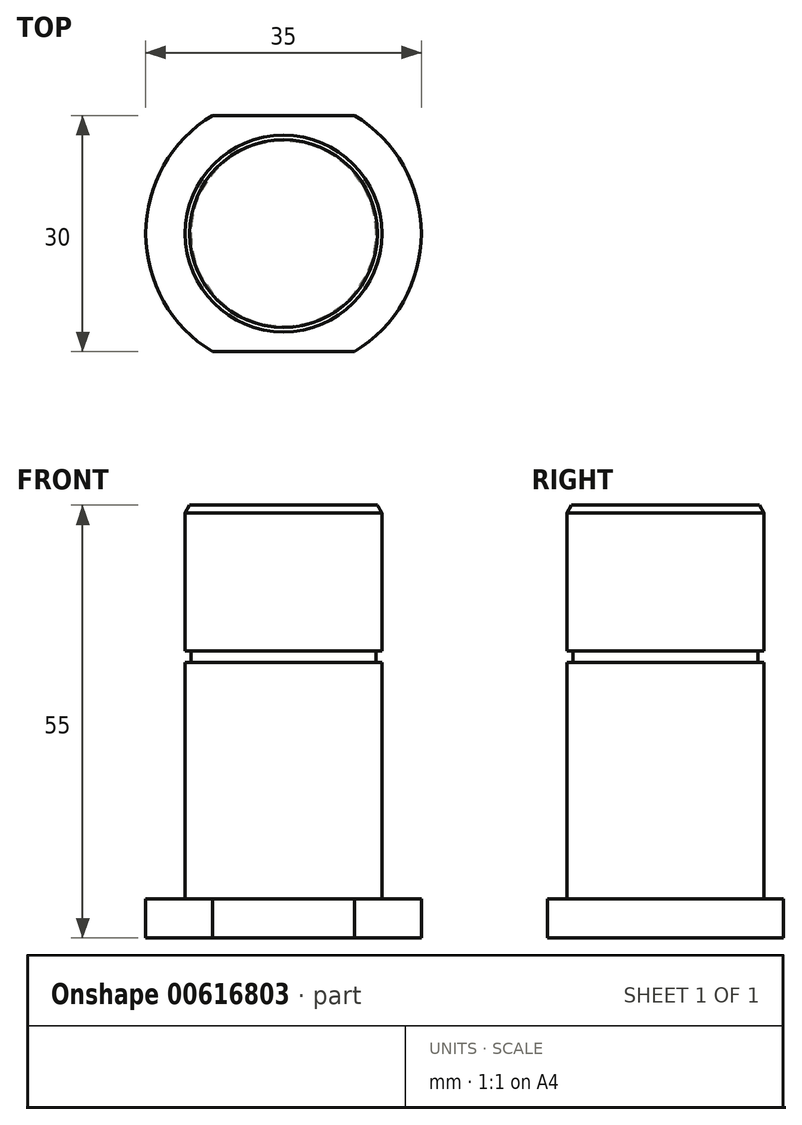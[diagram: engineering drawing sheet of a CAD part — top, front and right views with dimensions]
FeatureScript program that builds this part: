
annotation { "Feature Type Name" : "Feature", "Feature Type Description" : "" }
export const myFeature = defineFeature(function(context is Context, id is Id, definition is map)
    precondition{}
    {
        {
            var Q0;
            Q0=qCreatedBy(makeId("Top.planeOp"),FACE);
            var sketch = newSketch(context, id + "F0", { "sketchPlane" : qUnion([Q0])});
            skCircle(sketch, "E0", {"center": v(0, 0) * mm, "radius": 17.5 * mm});
            skSolve(sketch);
        }
        {
            var Q0;
            Q0 = qSketchRegion(id + "F0", true);
            extrude(context, id + "F1", {"entities" : qUnion([Q0]), "depth" : 5 * mm, "offsetDistance" : 25 * mm});
        }
        {
            var Q0;
            Q0=makeQuery(id+"F1.opExtrude","CAP_FACE",FACE,{"disambiguationData":[OSD([sQuery(id+"F0.wireOp",EDGE,"E0")])],"isStart":false});
            var sketch = newSketch(context, id + "F2", { "sketchPlane" : qUnion([Q0])});
            skCircle(sketch, "E1", {"center": v(0, 0) * mm, "radius": 12.5 * mm});
            skSolve(sketch);
        }
        {
            var Q0;
            Q0 = qSketchRegion(id + "F2", true);
            extrude(context, id + "F3", {"entities" : qUnion([Q0]), "operationType" : NewBodyOperationType.ADD, "depth" : 50 * mm, "offsetDistance" : 25 * mm});
        }
        {
            var Q0;
            Q0=makeQuery(id+"F1.opExtrude","CAP_FACE",FACE,{"disambiguationData":[OSD([sQuery(id+"F0.wireOp",EDGE,"E0")])],"isStart":true});
            var sketch = newSketch(context, id + "F4", { "sketchPlane" : qUnion([Q0])});
            skLineSegment(sketch, "E2.bottom", {"start": v(22.5, 15) * mm, "end": v(-22.5, 15) * mm});
            skLineSegment(sketch, "E2.top", {"start": v(22.5, -15) * mm, "end": v(-22.5, -15) * mm});
            skLineSegment(sketch, "E2.left", {"start": v(22.5, 15) * mm, "end": v(22.5, -15) * mm});
            skLineSegment(sketch, "E2.right", {"start": v(-22.5, 15) * mm, "end": v(-22.5, -15) * mm});
            skPoint(sketch, "E2.middle", {"position": v(0, 0) * mm});
            skLineSegment(sketch, "E3.bottom", {"start": v(27.5, 20) * mm, "end": v(-27.5, 20) * mm});
            skLineSegment(sketch, "E3.top", {"start": v(27.5, -20) * mm, "end": v(-27.5, -20) * mm});
            skLineSegment(sketch, "E3.left", {"start": v(27.5, 20) * mm, "end": v(27.5, -20) * mm});
            skLineSegment(sketch, "E3.right", {"start": v(-27.5, 20) * mm, "end": v(-27.5, -20) * mm});
            skSolve(sketch);
        }
        {
            var Q0;
            Q0 = qSketchRegion(id + "F4", true);
            extrude(context, id + "F5", {"entities" : qUnion([Q0]), "operationType" : NewBodyOperationType.REMOVE, "oppositeDirection" : true, "depth" : 25 * mm, "offsetDistance" : 25 * mm});
        }
        {
            var Q0;
            Q0=qCreatedBy(makeId("Right.planeOp"),FACE);
            var sketch = newSketch(context, id + "F6", { "sketchPlane" : qUnion([Q0])});
            skLineSegment(sketch, "E4", {"start": v(-11.75, 36.5) * mm, "end": v(-15.16, 36.5) * mm});
            skLineSegment(sketch, "E5", {"start": v(-15.16, 36.5) * mm, "end": v(-15.16, 35) * mm});
            skLineSegment(sketch, "E6", {"start": v(-15.16, 35) * mm, "end": v(-11.75, 35) * mm});
            skLineSegment(sketch, "E7", {"start": v(-11.75, 36.5) * mm, "end": v(-11.75, 35) * mm});
            skLineSegment(sketch, "E8", {"start": v(-12.5, 5) * mm, "end": v(-12.5, 50) * mm, "construction": true});
            skLineSegment(sketch, "E9", {"start": v(0, 26.16) * mm, "end": v(0, 34.14) * mm, "construction": true});
            skSolve(sketch);
        }
        {
            var Q0;
            Q0 = qSketchRegion(id + "F6", true);
            var Q1;
            Q1=sQuery(id+"F6.wireOp",EDGE,"E9");
            revolve(context, id + "F7", {"operationType" : NewBodyOperationType.REMOVE, "surfaceOperationType" : NewSurfaceOperationType.NEW, "entities" : qUnion([Q0]), "axis" : qUnion([Q1]), "revolveType" : RevolveType.FULL, "oppositeDirection" : true});
        }
        {
            var Q0;
            Q0=makeQuery(id+"F3.opExtrude","CAP_EDGE",EDGE,{"disambiguationData":[OSD([sQuery(id+"F2.wireOp",EDGE,"E1")])],"isStart":false});
            chamfer(context, id + "F8", {"entities" : qUnion([Q0]), "chamferType" : ChamferType.OFFSET_ANGLE, "width" : 1 * mm, "oppositeDirection" : false, "angle" : 30 * degree, "tangentPropagation" : true});
        }
    });
